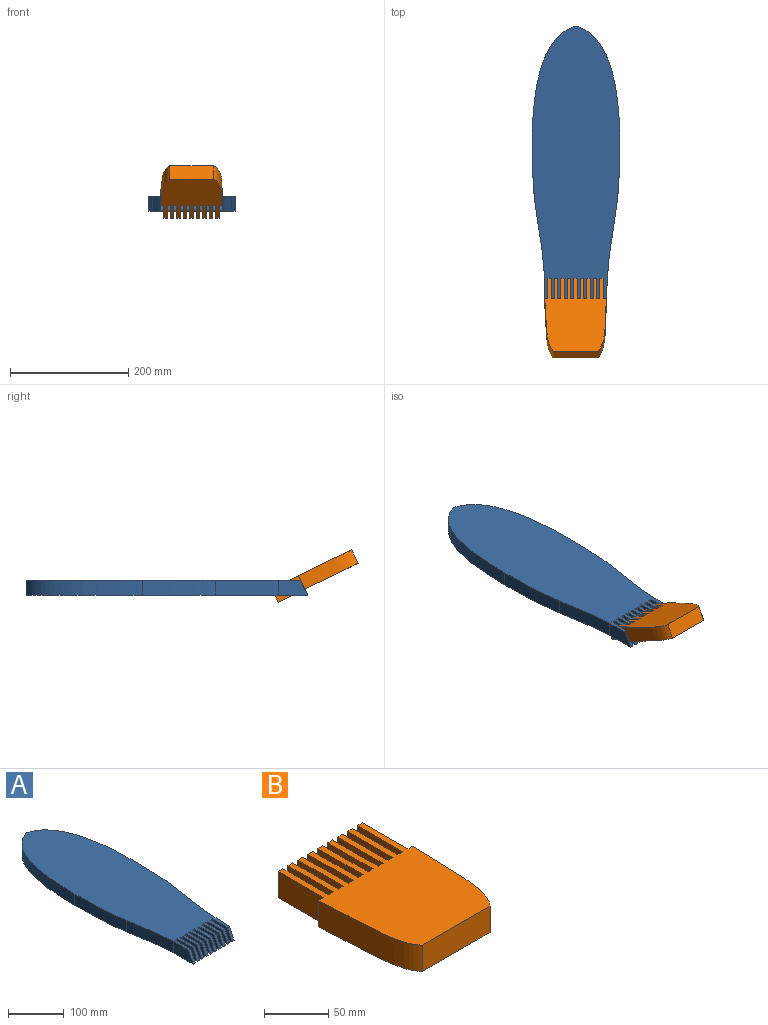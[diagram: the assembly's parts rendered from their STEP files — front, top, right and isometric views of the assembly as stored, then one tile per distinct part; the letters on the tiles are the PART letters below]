
ASSEMBLY  parts=2 mates=1
PART A: 56 faces, bbox 148x476x25 mm
  f0: plane 50x25mm, normal (-1,0,0), area 1106.7mm2, adj f15,f16,f17,f45,f46
  f1: plane 25x5.48mm, normal (0,-1,0), area 137mm2, adj f16,f17,f43,f44
  f2: plane 25x5.48mm, normal (0,-1,0), area 137mm2, adj f16,f17,f40,f42
  f3: plane 25x5.48mm, normal (0,-1,0), area 137mm2, adj f16,f17,f37,f39
  f4: plane 25x5.48mm, normal (0,-1,0), area 137mm2, adj f16,f17,f34,f36
  f5: plane 25x5.48mm, normal (0,-1,0), area 137mm2, adj f16,f17,f31,f33
  f6: plane 25x5.48mm, normal (0,-1,0), area 137mm2, adj f16,f17,f28,f30
  f7: plane 25x5.48mm, normal (0,-1,0), area 137mm2, adj f16,f17,f25,f27
  f8: plane 25x5.48mm, normal (0,-1,0), area 137mm2, adj f16,f17,f22,f24
  f9: plane 25x5.48mm, normal (0,-1,0), area 137mm2, adj f16,f17,f18,f21
  f10: extruded ~156x25mm, area 3780.3mm2, adj f11,f16,f17,f19,f55
  f11: extruded ~123.51x25mm, area 3097.5mm2, adj f10,f12,f16,f17
  f12: extruded ~196.49x73.98mm, area 5585.6mm2, adj f11,f13,f16,f17
  f13: extruded ~196.49x73.98mm, area 5585.6mm2, adj f12,f14,f16,f17
  f14: extruded ~123.51x25mm, area 3097.5mm2, adj f13,f15,f16,f17
  f15: extruded ~106x25mm, area 2672.6mm2, adj f0,f14,f16,f17
  f16: plane 465.65x147.97mm, normal (0,0,1), area 55491.7mm2, adj f0,f1,f2,f3,f4,f5,f6,f7
  f17: plane 476x147.97mm, normal (0,0,-1), area 56139.5mm2, adj f0,f1,f2,f3,f4,f5,f6,f7
  f18: plane 50x25mm, normal (-1,0,0), area 1106.7mm2, adj f9,f16,f17,f19,f55
  f19: plane 5.48x0.75mm, normal (0,-1,0), area 4.1mm2, adj f10,f17,f18,f55
  f20: plane 5.48x0.75mm, normal (0,-1,0), area 4.1mm2, adj f17,f21,f22,f54
  f21: plane 50x25mm, normal (1,0,0), area 1106.7mm2, adj f9,f16,f17,f20,f54
  f22: plane 50x25mm, normal (-1,0,0), area 1106.7mm2, adj f8,f16,f17,f20,f54
  f23: plane 5.48x0.75mm, normal (0,-1,0), area 4.1mm2, adj f17,f24,f25,f53
  f24: plane 50x25mm, normal (1,0,0), area 1106.7mm2, adj f8,f16,f17,f23,f53
  f25: plane 50x25mm, normal (-1,0,0), area 1106.7mm2, adj f7,f16,f17,f23,f53
  f26: plane 5.48x0.75mm, normal (0,-1,0), area 4.1mm2, adj f17,f27,f28,f52
  f27: plane 50x25mm, normal (1,0,0), area 1106.7mm2, adj f7,f16,f17,f26,f52
  f28: plane 50x25mm, normal (-1,0,0), area 1106.7mm2, adj f6,f16,f17,f26,f52
  f29: plane 5.48x0.75mm, normal (0,-1,0), area 4.1mm2, adj f17,f30,f31,f51
  f30: plane 50x25mm, normal (1,0,0), area 1106.7mm2, adj f6,f16,f17,f29,f51
  f31: plane 50x25mm, normal (-1,0,0), area 1106.7mm2, adj f5,f16,f17,f29,f51
  f32: plane 5.48x0.75mm, normal (0,-1,0), area 4.1mm2, adj f17,f33,f34,f50
  f33: plane 50x25mm, normal (1,0,0), area 1106.7mm2, adj f5,f16,f17,f32,f50
  f34: plane 50x25mm, normal (-1,0,0), area 1106.7mm2, adj f4,f16,f17,f32,f50
  f35: plane 5.48x0.75mm, normal (0,-1,0), area 4.1mm2, adj f17,f36,f37,f49
  f36: plane 50x25mm, normal (1,0,0), area 1106.7mm2, adj f4,f16,f17,f35,f49
  f37: plane 50x25mm, normal (-1,0,0), area 1106.7mm2, adj f3,f16,f17,f35,f49
  f38: plane 5.48x0.75mm, normal (0,-1,0), area 4.1mm2, adj f17,f39,f40,f48
  f39: plane 50x25mm, normal (1,0,0), area 1106.7mm2, adj f3,f16,f17,f38,f48
  f40: plane 50x25mm, normal (-1,0,0), area 1106.7mm2, adj f2,f16,f17,f38,f48
  f41: plane 5.48x0.75mm, normal (0,-1,0), area 4.1mm2, adj f17,f42,f43,f47
  f42: plane 50x25mm, normal (1,0,0), area 1106.7mm2, adj f2,f16,f17,f41,f47
  f43: plane 50x25mm, normal (-1,0,0), area 1106.7mm2, adj f1,f16,f17,f41,f47
  f44: plane 50x25mm, normal (1,0,0), area 1106.7mm2, adj f1,f16,f17,f45,f46
  f45: plane 5.48x0.75mm, normal (0,-1,0), area 4.1mm2, adj f0,f17,f44,f46
  f46: plane 24.25x11.82mm, normal (0,-0.9,0.44), area 147.8mm2, adj f0,f16,f44,f45
  f47: plane 24.25x11.82mm, normal (0,-0.9,0.44), area 147.8mm2, adj f16,f41,f42,f43
  f48: plane 24.25x11.82mm, normal (0,-0.9,0.44), area 147.8mm2, adj f16,f38,f39,f40
  f49: plane 24.25x11.82mm, normal (0,-0.9,0.44), area 147.8mm2, adj f16,f35,f36,f37
  f50: plane 24.25x11.82mm, normal (0,-0.9,0.44), area 147.8mm2, adj f16,f32,f33,f34
  f51: plane 24.25x11.82mm, normal (0,-0.9,0.44), area 147.8mm2, adj f16,f29,f30,f31
  f52: plane 24.25x11.82mm, normal (0,-0.9,0.44), area 147.8mm2, adj f16,f26,f27,f28
  f53: plane 24.25x11.82mm, normal (0,-0.9,0.44), area 147.8mm2, adj f16,f23,f24,f25
  f54: plane 24.25x11.82mm, normal (0,-0.9,0.44), area 147.8mm2, adj f16,f20,f21,f22
  f55: plane 24.25x11.82mm, normal (0,-0.9,0.44), area 148.7mm2, adj f10,f16,f18,f19
PART B: 42 faces, bbox 104.1x150x25 mm
  f0: plane 25x5.48mm, normal (0,1,0), area 137mm2, adj f1,f39,f40,f41
  f1: plane 50x25mm, normal (1,0,0), area 1250mm2, adj f0,f2,f40,f41
  f2: plane 25x5.48mm, normal (0,1,0), area 137mm2, adj f1,f3,f40,f41
  f3: plane 50x25mm, normal (-1,0,0), area 1250mm2, adj f2,f4,f40,f41
  f4: plane 25x5.48mm, normal (0,1,0), area 137mm2, adj f3,f5,f40,f41
  f5: plane 50x25mm, normal (1,0,0), area 1250mm2, adj f4,f6,f40,f41
  f6: plane 25x5.48mm, normal (0,1,0), area 137mm2, adj f5,f7,f40,f41
  f7: plane 50x25mm, normal (-1,0,0), area 1250mm2, adj f6,f8,f40,f41
  f8: plane 25x5.48mm, normal (0,1,0), area 137mm2, adj f7,f9,f40,f41
  f9: plane 50x25mm, normal (1,0,0), area 1250mm2, adj f8,f10,f40,f41
  f10: plane 25x5.48mm, normal (0,1,0), area 137mm2, adj f9,f11,f40,f41
  f11: plane 50x25mm, normal (-1,0,0), area 1250mm2, adj f10,f12,f40,f41
  f12: plane 25x5.48mm, normal (0,1,0), area 137mm2, adj f11,f13,f40,f41
  f13: plane 50x25mm, normal (1,0,0), area 1250mm2, adj f12,f14,f40,f41
  f14: plane 25x5.48mm, normal (0,1,0), area 137mm2, adj f13,f15,f40,f41
  f15: plane 50x25mm, normal (-1,0,0), area 1250mm2, adj f14,f16,f40,f41
  f16: plane 25x5.48mm, normal (0,1,0), area 137mm2, adj f15,f17,f40,f41
  f17: plane 50x25mm, normal (1,0,0), area 1250mm2, adj f16,f18,f40,f41
  f18: plane 25x5.48mm, normal (0,1,0), area 137mm2, adj f17,f19,f40,f41
  f19: plane 50x25mm, normal (-1,0,0), area 1250mm2, adj f18,f20,f40,f41
  f20: plane 25x5.48mm, normal (0,1,0), area 137mm2, adj f19,f21,f40,f41
  f21: extruded ~100x25mm, area 2564.4mm2, adj f20,f22,f40,f41
  f22: plane 74.11x25mm, normal (0,-1,0), area 1852.7mm2, adj f21,f23,f40,f41
  f23: extruded ~100x25mm, area 2570.6mm2, adj f22,f24,f40,f41
  f24: plane 25x5.48mm, normal (0,1,0), area 137mm2, adj f23,f25,f40,f41
  f25: plane 50x25mm, normal (1,0,0), area 1250mm2, adj f24,f26,f40,f41
  f26: plane 25x5.48mm, normal (0,1,0), area 137mm2, adj f25,f27,f40,f41
  f27: plane 50x25mm, normal (-1,0,0), area 1250mm2, adj f26,f28,f40,f41
  f28: plane 25x5.48mm, normal (0,1,0), area 137mm2, adj f27,f29,f40,f41
  f29: plane 50x25mm, normal (1,0,0), area 1250mm2, adj f28,f30,f40,f41
  f30: plane 25x5.48mm, normal (0,1,0), area 137mm2, adj f29,f31,f40,f41
  f31: plane 50x25mm, normal (-1,0,0), area 1250mm2, adj f30,f32,f40,f41
  f32: plane 25x5.48mm, normal (0,1,0), area 137mm2, adj f31,f33,f40,f41
  f33: plane 50x25mm, normal (1,0,0), area 1250mm2, adj f32,f34,f40,f41
  f34: plane 25x5.48mm, normal (0,1,0), area 137mm2, adj f33,f35,f40,f41
  f35: plane 50x25mm, normal (-1,0,0), area 1250mm2, adj f34,f36,f40,f41
  f36: plane 25x5.48mm, normal (0,1,0), area 137mm2, adj f35,f37,f40,f41
  f37: plane 50x25mm, normal (1,0,0), area 1250mm2, adj f36,f38,f40,f41
  f38: plane 25x5.48mm, normal (0,1,0), area 137mm2, adj f37,f39,f40,f41
  f39: plane 50x25mm, normal (-1,0,0), area 1250mm2, adj f0,f38,f40,f41
  f40: plane 150x104.11mm, normal (0,0,1), area 12192.1mm2, adj f0,f1,f2,f3,f4,f5,f6,f7
  f41: plane 150x104.11mm, normal (0,0,-1), area 12192.1mm2, adj f0,f1,f2,f3,f4,f5,f6,f7
PLACE A rot(axis=(-1,0,0),0deg) t=(-20.37,-40.34,-15.59)mm
PLACE B rot(axis=(-1,0,0),26deg) t=(-21.21,-337.48,5.54)mm
MATE parallel B.f24 <-> A.f55  axis (0,0.9,-0.44) through (28.1,-304.05,17.06)mm
